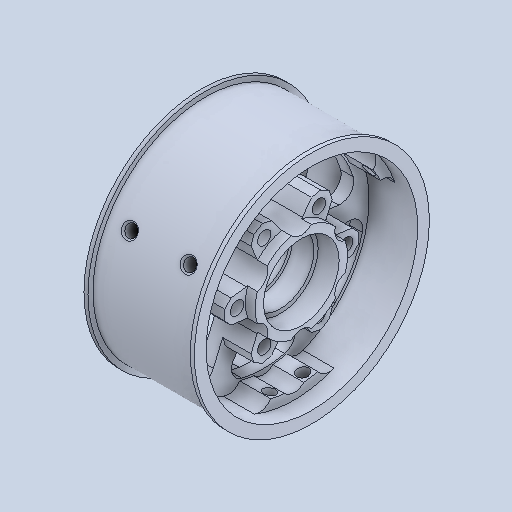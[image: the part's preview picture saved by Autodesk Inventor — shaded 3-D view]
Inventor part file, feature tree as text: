
AUTODESK INVENTOR PART (.ipt)
format: ipt  version: 2023.2 (Build 272271000, 271)  size: 372,224 bytes
history: native  units: in
note: dims shown in document units (in); Inventor stores cm internally (conversion verified against a paired STEP export)
features: mirror x1
ambient origin geometry x8: Origin, YZ Plane, XZ Plane, XY Plane, X Axis, Y Axis, Z Axis, Center Point
bodies: Solid1 (feature_tree)
feature tree (1):
  mirror  "Mirror3"
